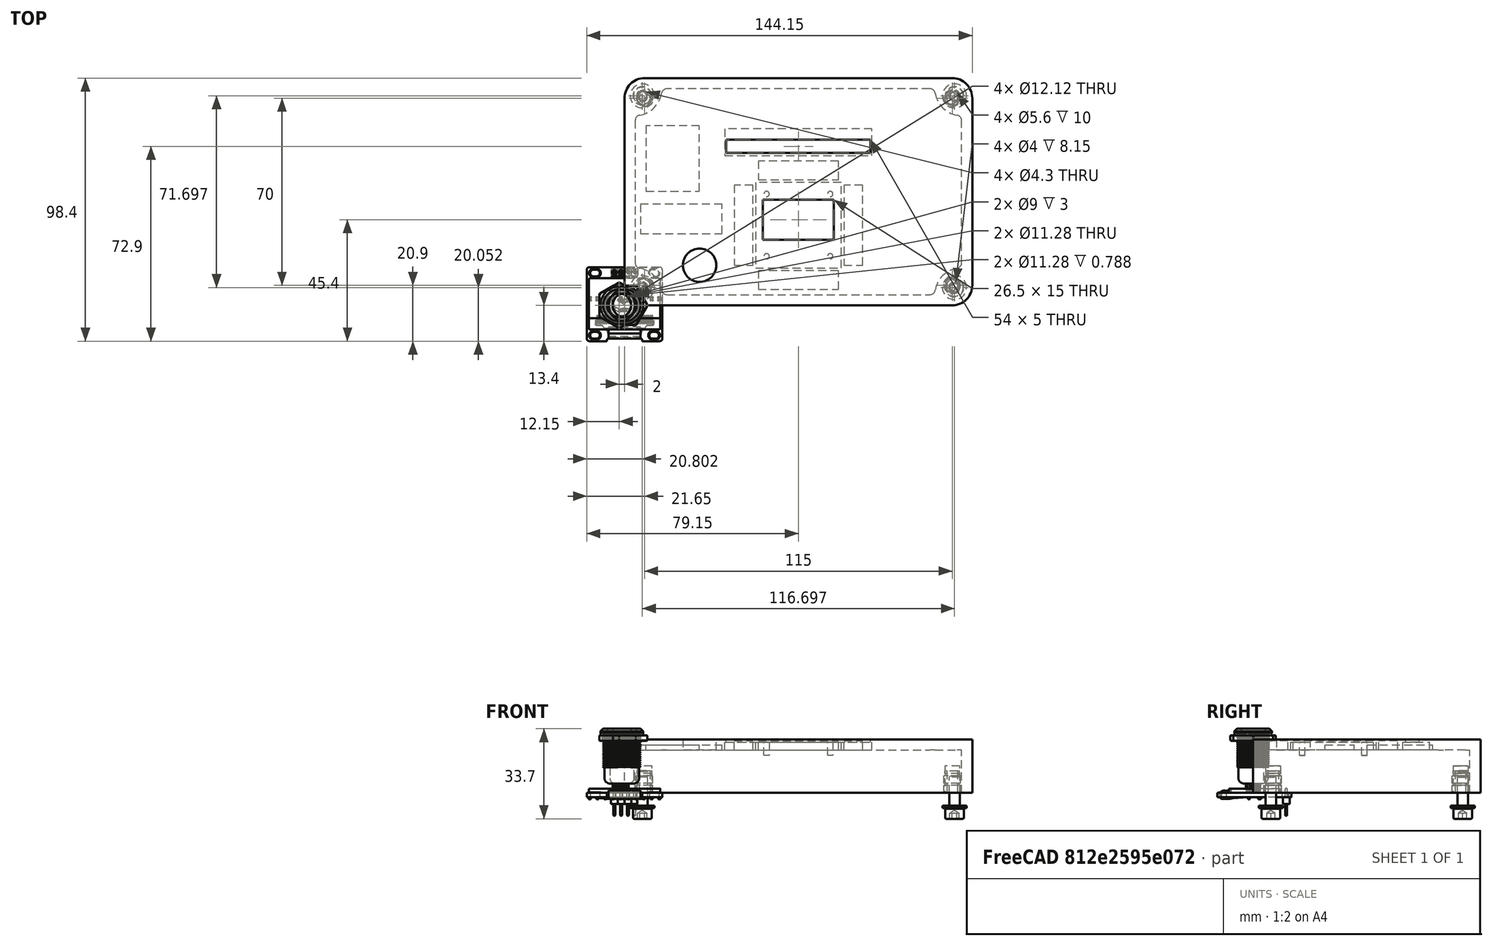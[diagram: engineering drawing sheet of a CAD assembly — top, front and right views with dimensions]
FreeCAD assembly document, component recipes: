
FREECAD ASSEMBLY — COMPONENT RECIPES ("FirstDraft")

This assembly document has 5 components, labeled P0..P4 below (a component is one placed body or linked part). 2 of them carry a construction recipe — the FreeCAD feature program that regenerates the part from scratch, quoted from this document or its linked companion documents; the rest are supplied as boundary geometry only. No exploded tour is included for this assembly.
COMPONENT P0 — geometry summary ("Assembly"; no construction recipe available for this part):
  bounding box: 130.0 x 85.0 x 30.0 mm
  tessellated surface: 3,268 triangles
  volume: 81614518091937392678094543782171779412625645482801444618089581424482953678321251914316762090945118208 mm^3 (24619764130297853257637544613362442512160034095616427615261483626677733875047030041199137435680768% of its bounding box)
  symmetry: mirror-symmetric across its x mid-plane
COMPONENT P1 — recipe-attached ("Base", modeled in this document).
Construction recipe (the document's own serialized feature program — sketch geometry with constraints, then the solid features built on it; lengths are millimeters unless a unit is written):

FEATURE [PartDesign::ShapeBinder] ShapeBinder
  Support = -> [Pocket]
  TraceSupport = true
FEATURE [Sketcher::SketchObject] Sketch010
  ExternalGeometry = -> [ShapeBinder]
  FullyConstrained = true
  MapMode = 5
  Placement = pos=(0,0,0) rot=(1,0,0;3.14159rad)
  Support = -> [ShapeBinder]
  sketch-geometry (23):
    g0: GeomPoint X=5 Y=-5 Z=0
    g1: GeomPoint X=125 Y=-80 Z=0
    g2: GeomPoint X=65 Y=-42.5 Z=0
    g3: ArcOfCircle CenterX=5 CenterY=-80 CenterZ=0 NormalX=0 NormalY=0 NormalZ=1 AngleXU=0 Radius=10 StartAngle=0.167448 EndAngle=1.40335
    g4: ArcOfCircle CenterX=7 CenterY=-68.1678 CenterZ=0 NormalX=0 NormalY=0 NormalZ=1 AngleXU=0 Radius=2 StartAngle=3.14159 EndAngle=4.54494
    g5: ArcOfCircle CenterX=5 CenterY=-5 CenterZ=0 NormalX=0 NormalY=0 NormalZ=1 AngleXU=0 Radius=10 StartAngle=1.40335 EndAngle=6.11574
    g6: ArcOfCircle CenterX=125 CenterY=-5 CenterZ=0 NormalX=0 NormalY=0 NormalZ=1 AngleXU=0 Radius=10 StartAngle=3.30904 EndAngle=4.54494
    g7: ArcOfCircle CenterX=125 CenterY=-80 CenterZ=0 NormalX=0 NormalY=0 NormalZ=1 AngleXU=0 Radius=10 StartAngle=1.73824 EndAngle=2.97414
    g8: LineSegment StartX=5 StartY=-80 StartZ=0 EndX=125 EndY=-80 EndZ=0
    g9: LineSegment StartX=125 StartY=-80 StartZ=0 EndX=125 EndY=-5 EndZ=0
    g10: LineSegment StartX=5 StartY=-5 StartZ=0 EndX=5 EndY=-80 EndZ=0
    g11: ArcOfCircle CenterX=7 CenterY=6.83216 CenterZ=0 NormalX=0 NormalY=0 NormalZ=1 AngleXU=0 Radius=2 StartAngle=4.54494 EndAngle=9.42478
    g12: ArcOfCircle CenterX=123 CenterY=-16.8322 CenterZ=0 NormalX=0 NormalY=0 NormalZ=1 AngleXU=0 Radius=2 StartAngle=4e-16 EndAngle=1.40335
    g13: ArcOfCircle CenterX=16.8322 CenterY=-7 CenterZ=0 NormalX=0 NormalY=0 NormalZ=1 AngleXU=0 Radius=2 StartAngle=1.5708 EndAngle=2.97414
    g14: ArcOfCircle CenterX=113.168 CenterY=-7 CenterZ=0 NormalX=0 NormalY=0 NormalZ=1 AngleXU=0 Radius=2 StartAngle=0.167448 EndAngle=1.5708
    g15: ArcOfCircle CenterX=123 CenterY=-68.1678 CenterZ=0 NormalX=0 NormalY=0 NormalZ=1 AngleXU=0 Radius=2 StartAngle=4.87984 EndAngle=6.28319
    g16: ArcOfCircle CenterX=113.168 CenterY=-78 CenterZ=0 NormalX=0 NormalY=0 NormalZ=1 AngleXU=0 Radius=2 StartAngle=4.71239 EndAngle=6.11574
    g17: ArcOfCircle CenterX=16.8322 CenterY=-78 CenterZ=0 NormalX=0 NormalY=0 NormalZ=1 AngleXU=0 Radius=2 StartAngle=3.30904 EndAngle=4.71239
    g18: LineSegment StartX=5 StartY=-5 StartZ=0 EndX=125 EndY=-5 EndZ=0
    g19: LineSegment StartX=5 StartY=6.83216 StartZ=0 EndX=5 EndY=-68.1678 EndZ=0
    g20: LineSegment StartX=125 StartY=-68.1678 StartZ=0 EndX=125 EndY=-16.8322 EndZ=0
    g21: LineSegment StartX=113.168 StartY=-5 StartZ=0 EndX=16.8322 EndY=-5 EndZ=0
    g22: LineSegment StartX=16.8322 StartY=-80 StartZ=0 EndX=113.168 EndY=-80 EndZ=0
  constraints (54):
    c: Tangent(g3,g4) = 1.5708
    c: Coincident(g7,g1)
    c: Coincident(g8,g9)
    c: Coincident(g10,g8)
    c: Horizontal(g8)
    c: Vertical(g9)
    c: Vertical(g10)
    c: Coincident(g8,g3)
    c: Coincident(g9,g6)
    c: Coincident(g0,g5)
    c: Symmetric(g3,g6,g2)
    c: Tangent(g5,g11) = 1.5708
    c: Tangent(g6,g12) = 1.5708
    c: Tangent(g5,g13) = 1.5708
    c: Tangent(g6,g14) = 1.5708
    c: Tangent(g7,g15) = 1.5708
    c: Tangent(g7,g16) = 1.5708
    c: Equal(g3,g5)
    c: Equal(g5,g6)
    c: Equal(g6,g7)
    c: Radius(g3) = 10
    c: Equal(g4,g13)
    c: Equal(g13,g11)
    c: Equal(g11,g14)
    c: Equal(g12,g15)
    c: Tangent(g16,g8) = -1.5708
    c: Tangent(g4,g10) = -1.5708
    c: Coincident(g8,g7)
    c: Tangent(g17,g8) = -1.5708
    c: Tangent(g17,g3) = 1.5708
    c: Radius(g17) = 2
    c: Tangent(g12,g9) = -1.5708
    c: Tangent(g15,g9) = -1.5708
    c: Tangent(g11,g10) = -1.5708
    c: Coincident(g18,g5)
    c: Horizontal(g18)
    c: Coincident(g18,g6)
    c: Coincident(g10,g5)
    c: Tangent(g13,g18) = 1.5708
    c: Tangent(g14,g18) = 1.5708
    c: Equal(g11,g12)
    c: Equal(g14,g17)
    c: Equal(g17,g16)
    c: Symmetric(g-3,g-5,g2)
    c: Coincident(g19,g11)
    c: Coincident(g19,g4)
    c: Coincident(g20,g15)
    c: Coincident(g20,g12)
    c: Coincident(g21,g14)
    c: Coincident(g21,g13)
    c: DistanceY(g5,g-4) = 1
    c: DistanceX(g-5,g11) = 1
    c: Coincident(g22,g17)
    c: Coincident(g22,g16)
FEATURE [Sketcher::SketchObject] Sketch011
  ExternalGeometry = -> [ShapeBinder]
  FullyConstrained = true
  MapMode = 5
  Placement = pos=(0,0,0) rot=(1,0,0;3.14159rad)
  Support = -> [ShapeBinder]
  sketch-geometry (12):
    g0: LineSegment StartX=7.5 StartY=0 StartZ=0 EndX=122.5 EndY=0 EndZ=0
    g1: LineSegment StartX=130 StartY=-7.5 StartZ=0 EndX=130 EndY=-77.5 EndZ=0
    g2: LineSegment StartX=122.5 StartY=-85 StartZ=0 EndX=7.5 EndY=-85 EndZ=0
    g3: LineSegment StartX=0 StartY=-77.5 StartZ=0 EndX=0 EndY=-7.5 EndZ=0
    g4: ArcOfCircle CenterX=7.5 CenterY=-7.5 CenterZ=0 NormalX=0 NormalY=0 NormalZ=1 AngleXU=0 Radius=7.5 StartAngle=1.5708 EndAngle=3.14159
    g5: GeomPoint X=0 Y=0 Z=0
    g6: ArcOfCircle CenterX=122.5 CenterY=-7.5 CenterZ=0 NormalX=0 NormalY=0 NormalZ=1 AngleXU=0 Radius=7.5 StartAngle=0 EndAngle=1.5708
    g7: GeomPoint X=130 Y=0 Z=0
    g8: ArcOfCircle CenterX=122.5 CenterY=-77.5 CenterZ=0 NormalX=0 NormalY=0 NormalZ=1 AngleXU=0 Radius=7.5 StartAngle=4.71239 EndAngle=6.28319
    g9: GeomPoint X=130 Y=-85 Z=0
    g10: ArcOfCircle CenterX=7.5 CenterY=-77.5 CenterZ=0 NormalX=0 NormalY=0 NormalZ=1 AngleXU=0 Radius=7.5 StartAngle=3.14159 EndAngle=4.71239
    g11: GeomPoint X=0 Y=-85 Z=0
  constraints (23):
    c: Horizontal(g0)
    c: Vertical(g1)
    c: Vertical(g3)
    c: Coincident(g5,g-1)
    c: PointOnObject(g5,g3)
    c: Tangent(g0,g4) = 1.5708
    c: Tangent(g3,g4) = 1.5708
    c: PointOnObject(g7,g1)
    c: PointOnObject(g7,g0)
    c: Tangent(g1,g6) = 1.5708
    c: Tangent(g0,g6) = 1.5708
    c: PointOnObject(g9,g1)
    c: PointOnObject(g9,g2)
    c: Tangent(g1,g8) = 1.5708
    c: Tangent(g2,g8) = 1.5708
    c: PointOnObject(g11,g2)
    c: PointOnObject(g11,g3)
    c: Tangent(g2,g10) = 1.5708
    c: Tangent(g3,g10) = 1.5708
    c: Coincident(g2,g-4)
    c: Coincident(g2,g-4)
    c: Coincident(g-3,g1)
    c: Coincident(g0,g-5)
FEATURE [PartDesign::Pad] Pad003
  Direction = (0,0,-1)
  Length = 10
  Length2 = 10
  Profile = -> Sketch011
  ReferenceAxis = -> Sketch011 [N_Axis]
  Type = 0
FEATURE [PartDesign::Pocket] Pocket005
  BaseFeature = -> Pad003
  Direction = (0,0,1)
  Length = 7
  Length2 = 5
  Profile = -> Sketch010
  ReferenceAxis = -> Sketch010 [N_Axis]
  Reversed = true
  Type = 0
FEATURE [Sketcher::SketchObject] Sketch012
  ExternalGeometry = -> [ShapeBinder]
  FullyConstrained = true
  MapMode = 5
  Placement = pos=(0,0,-10) rot=(1,0,0;3.14159rad)
  Support = -> [Pocket005]
  sketch-geometry (4):
    g0: Circle CenterX=6.65146 CenterY=-6.65148 CenterZ=0 NormalX=0 NormalY=0 NormalZ=1 AngleXU=0 Radius=2.8
    g1: Circle CenterX=123.349 CenterY=-6.65148 CenterZ=0 NormalX=0 NormalY=0 NormalZ=1 AngleXU=0 Radius=2.8
    g2: Circle CenterX=123.349 CenterY=-78.3485 CenterZ=0 NormalX=0 NormalY=0 NormalZ=1 AngleXU=0 Radius=2.8
    g3: Circle CenterX=6.65146 CenterY=-78.3485 CenterZ=0 NormalX=0 NormalY=0 NormalZ=1 AngleXU=0 Radius=2.8
  constraints (8):
    c: Coincident(g1,g-4)
    c: Coincident(g2,g-5)
    c: Coincident(g3,g-6)
    c: Coincident(g0,g-3)
    c: Equal(g0,g-3)
    c: Equal(g0,g1)
    c: Equal(g1,g2)
    c: Equal(g2,g3)
FEATURE [PartDesign::Hole] Hole
  BaseFeature = -> Pocket005
  CustomThreadClearance = 0
  Depth = 314.401
  DepthType = 1
  Diameter = 4.5
  DrillForDepth = false
  DrillPoint = 1
  DrillPointAngle = 118
  HoleCutCountersinkAngle = 90
  HoleCutCustomValues = false
  HoleCutDepth = 5.2
  HoleCutDiameter = 10
  HoleCutType = 12
  ModelThread = false
  Profile = -> Sketch012
  Tapered = false
  TaperedAngle = 90
  ThreadClass = 0
  ThreadDepth = 314.401
  ThreadDepthType = 0
  ThreadDirection = 0
  ThreadFit = 0
  ThreadSize = 11
  ThreadType = 1
  Threaded = false
  UseCustomThreadClearance = false
FEATURE [Sketcher::SketchObject] Sketch013
  ExternalGeometry = -> [ShapeBinder]
  FullyConstrained = true
  MapMode = 5
  Placement = pos=(0,0,0) rot=(1,0,0;3.14159rad)
  Support = -> [ShapeBinder]
  sketch-geometry (46):
    g0: GeomPoint X=5 Y=-28.6643 Z=0
    g1: GeomPoint X=125 Y=-80 Z=0
    g2: GeomPoint X=65 Y=-54.3322 Z=0
    g3: ArcOfCircle CenterX=5 CenterY=-80 CenterZ=0 NormalX=0 NormalY=0 NormalZ=1 AngleXU=0 Radius=10 StartAngle=0.167448 EndAngle=1.40335
    g4: ArcOfCircle CenterX=7 CenterY=-68.1678 CenterZ=0 NormalX=0 NormalY=0 NormalZ=1 AngleXU=0 Radius=2 StartAngle=3.14159 EndAngle=4.54494
    g5: ArcOfCircle CenterX=5 CenterY=-28.6643 CenterZ=0 NormalX=0 NormalY=0 NormalZ=1 AngleXU=0 Radius=10 StartAngle=4.87984 EndAngle=6.11574
    g6: ArcOfCircle CenterX=125 CenterY=-28.6643 CenterZ=0 NormalX=0 NormalY=0 NormalZ=1 AngleXU=0 Radius=10 StartAngle=3.30904 EndAngle=4.54494
    g7: ArcOfCircle CenterX=125 CenterY=-80 CenterZ=0 NormalX=0 NormalY=0 NormalZ=1 AngleXU=0 Radius=10 StartAngle=1.73824 EndAngle=2.97414
    g8: LineSegment StartX=5 StartY=-80 StartZ=0 EndX=125 EndY=-80 EndZ=0
    g9: LineSegment StartX=125 StartY=-80 StartZ=0 EndX=125 EndY=-28.6643 EndZ=0
    g10: LineSegment StartX=5 StartY=-28.6643 StartZ=0 EndX=5 EndY=-80 EndZ=0
    g11: ArcOfCircle CenterX=7 CenterY=-40.4965 CenterZ=0 NormalX=0 NormalY=0 NormalZ=1 AngleXU=0 Radius=2 StartAngle=1.73824 EndAngle=3.14159
    g12: ArcOfCircle CenterX=123 CenterY=-40.4965 CenterZ=0 NormalX=0 NormalY=0 NormalZ=1 AngleXU=0 Radius=2 StartAngle=-9e-16 EndAngle=1.40335
    g13: ArcOfCircle CenterX=16.8322 CenterY=-30.6643 CenterZ=0 NormalX=0 NormalY=0 NormalZ=1 AngleXU=0 Radius=2 StartAngle=1.5708 EndAngle=2.97414
    g14: ArcOfCircle CenterX=113.168 CenterY=-30.6643 CenterZ=0 NormalX=0 NormalY=0 NormalZ=1 AngleXU=0 Radius=2 StartAngle=0.167448 EndAngle=1.5708
    g15: ArcOfCircle CenterX=123 CenterY=-68.1678 CenterZ=0 NormalX=0 NormalY=0 NormalZ=1 AngleXU=0 Radius=2 StartAngle=4.87984 EndAngle=6.28319
    g16: ArcOfCircle CenterX=113.168 CenterY=-78 CenterZ=0 NormalX=0 NormalY=0 NormalZ=1 AngleXU=0 Radius=2 StartAngle=4.71239 EndAngle=6.11574
    g17: ArcOfCircle CenterX=16.8322 CenterY=-78 CenterZ=0 NormalX=0 NormalY=0 NormalZ=1 AngleXU=0 Radius=2 StartAngle=3.30904 EndAngle=4.71239
    g18: LineSegment StartX=5 StartY=-28.6643 StartZ=0 EndX=125 EndY=-28.6643 EndZ=0
    g19: LineSegment StartX=5 StartY=-40.4965 StartZ=0 EndX=5 EndY=-68.1678 EndZ=0
    g20: LineSegment StartX=125 StartY=-68.1678 StartZ=0 EndX=125 EndY=-40.4965 EndZ=0
    g21: LineSegment StartX=113.168 StartY=-28.6643 StartZ=0 EndX=16.8322 EndY=-28.6643 EndZ=0
    g22: LineSegment StartX=16.8322 StartY=-80 StartZ=0 EndX=113.168 EndY=-80 EndZ=0
    g23: GeomPoint X=4 Y=-27.6643 Z=0
    g24: GeomPoint X=126 Y=-81 Z=0
    g25: GeomPoint X=65 Y=-54.3322 Z=0
    g26: ArcOfCircle CenterX=4 CenterY=-81 CenterZ=0 NormalX=0 NormalY=0 NormalZ=1 AngleXU=0 Radius=10 StartAngle=0.167448 EndAngle=1.40335
    g27: ArcOfCircle CenterX=6 CenterY=-69.1678 CenterZ=0 NormalX=0 NormalY=0 NormalZ=1 AngleXU=0 Radius=2 StartAngle=3.14159 EndAngle=4.54494
    g28: ArcOfCircle CenterX=4 CenterY=-27.6643 CenterZ=0 NormalX=0 NormalY=0 NormalZ=1 AngleXU=0 Radius=10 StartAngle=1.40335 EndAngle=6.11574
    g29: ArcOfCircle CenterX=126 CenterY=-27.6643 CenterZ=0 NormalX=0 NormalY=0 NormalZ=1 AngleXU=0 Radius=10 StartAngle=3.30904 EndAngle=4.54494
    g30: ArcOfCircle CenterX=126 CenterY=-81 CenterZ=0 NormalX=0 NormalY=0 NormalZ=1 AngleXU=0 Radius=10 StartAngle=1.73824 EndAngle=2.97414
    g31: LineSegment StartX=4 StartY=-81 StartZ=0 EndX=126 EndY=-81 EndZ=0
    g32: LineSegment StartX=126 StartY=-81 StartZ=0 EndX=126 EndY=-27.6643 EndZ=0
    g33: LineSegment StartX=4 StartY=-27.6643 StartZ=0 EndX=4 EndY=-81 EndZ=0
    g34: ArcOfCircle CenterX=6 CenterY=-15.8322 CenterZ=0 NormalX=0 NormalY=0 NormalZ=1 AngleXU=0 Radius=2 StartAngle=4.54494 EndAngle=9.42478
    g35: ArcOfCircle CenterX=124 CenterY=-39.4965 CenterZ=0 NormalX=0 NormalY=0 NormalZ=1 AngleXU=0 Radius=2 StartAngle=-9e-16 EndAngle=1.40335
    g36: ArcOfCircle CenterX=15.8322 CenterY=-29.6643 CenterZ=0 NormalX=0 NormalY=0 NormalZ=1 AngleXU=0 Radius=2 StartAngle=1.5708 EndAngle=2.97414
    g37: ArcOfCircle CenterX=114.168 CenterY=-29.6643 CenterZ=0 NormalX=0 NormalY=0 NormalZ=1 AngleXU=0 Radius=2 StartAngle=0.167448 EndAngle=1.5708
    g38: ArcOfCircle CenterX=124 CenterY=-69.1678 CenterZ=0 NormalX=0 NormalY=0 NormalZ=1 AngleXU=0 Radius=2 StartAngle=4.87984 EndAngle=6.28319
    g39: ArcOfCircle CenterX=114.168 CenterY=-79 CenterZ=0 NormalX=0 NormalY=0 NormalZ=1 AngleXU=0 Radius=2 StartAngle=4.71239 EndAngle=6.11574
    g40: ArcOfCircle CenterX=15.8322 CenterY=-79 CenterZ=0 NormalX=0 NormalY=0 NormalZ=1 AngleXU=0 Radius=2 StartAngle=3.30904 EndAngle=4.71239
    g41: LineSegment StartX=4 StartY=-27.6643 StartZ=0 EndX=126 EndY=-27.6643 EndZ=0
    g42: LineSegment StartX=4 StartY=-15.8322 StartZ=0 EndX=4 EndY=-69.1678 EndZ=0
    g43: LineSegment StartX=126 StartY=-69.1678 StartZ=0 EndX=126 EndY=-39.4965 EndZ=0
    g44: LineSegment StartX=114.168 StartY=-27.6643 StartZ=0 EndX=15.8322 EndY=-27.6643 EndZ=0
    g45: LineSegment StartX=15.8322 StartY=-81 StartZ=0 EndX=114.168 EndY=-81 EndZ=0
  constraints (107):
    c: Tangent(g3,g4) = 1.5708
    c: Coincident(g7,g1)
    c: Coincident(g8,g9)
    c: Coincident(g10,g8)
    c: Horizontal(g8)
    c: Vertical(g9)
    c: Vertical(g10)
    c: Coincident(g8,g3)
    c: Coincident(g9,g6)
    c: Coincident(g0,g5)
    c: Symmetric(g3,g6,g2)
    c: Tangent(g5,g11) = 1.5708
    c: Tangent(g6,g12) = 1.5708
    c: Tangent(g5,g13) = 1.5708
    c: Tangent(g6,g14) = 1.5708
    c: Tangent(g7,g15) = 1.5708
    c: Tangent(g7,g16) = 1.5708
    c: Equal(g3,g5)
    c: Equal(g5,g6)
    c: Equal(g6,g7)
    c: Radius(g3) = 10
    c: Equal(g4,g13)
    c: Equal(g13,g11)
    c: Equal(g11,g14)
    c: Equal(g12,g15)
    c: Tangent(g16,g8) = -1.5708
    c: Tangent(g4,g10) = -1.5708
    c: Coincident(g8,g7)
    c: Tangent(g17,g8) = -1.5708
    c: Tangent(g17,g3) = 1.5708
    c: Radius(g17) = 2
    c: Tangent(g12,g9) = -1.5708
    c: Tangent(g15,g9) = -1.5708
    c: Tangent(g11,g10) = -1.5708
    c: Coincident(g18,g5)
    c: Horizontal(g18)
    c: Coincident(g18,g6)
    c: Coincident(g10,g5)
    c: Tangent(g13,g18) = 1.5708
    c: Tangent(g14,g18) = 1.5708
    c: Equal(g11,g12)
    c: Equal(g14,g17)
    c: Equal(g17,g16)
    c: Coincident(g19,g11)
    c: Coincident(g19,g4)
    c: Coincident(g20,g15)
    c: Coincident(g20,g12)
    c: Coincident(g21,g14)
    c: Coincident(g21,g13)
    c: Coincident(g22,g17)
    c: Coincident(g22,g16)
    c: Tangent(g26,g27) = 1.5708
    c: Coincident(g30,g24)
    c: Coincident(g31,g32)
    c: Coincident(g33,g31)
    c: Horizontal(g31)
    c: Vertical(g32)
    c: Vertical(g33)
    c: Coincident(g31,g26)
    c: Coincident(g32,g29)
    c: Coincident(g23,g28)
    c: Symmetric(g26,g29,g25)
    c: Tangent(g28,g34) = 1.5708
    c: Tangent(g29,g35) = 1.5708
    c: Tangent(g28,g36) = 1.5708
    c: Tangent(g29,g37) = 1.5708
    c: Tangent(g30,g38) = 1.5708
    c: Tangent(g30,g39) = 1.5708
    c: Equal(g26,g28)
    c: Equal(g28,g29)
    c: Equal(g29,g30)
    c: Radius(g26) = 10
    c: Equal(g27,g36)
    c: Equal(g36,g34)
    c: Equal(g34,g37)
    c: Equal(g35,g38)
    c: Tangent(g39,g31) = -1.5708
    c: Tangent(g27,g33) = -1.5708
    c: Coincident(g31,g30)
    c: Tangent(g40,g31) = -1.5708
    c: Tangent(g40,g26) = 1.5708
    c: Radius(g40) = 2
    c: Tangent(g35,g32) = -1.5708
    c: Tangent(g38,g32) = -1.5708
    c: Tangent(g34,g33) = -1.5708
    c: Coincident(g41,g28)
    c: Horizontal(g41)
    c: Coincident(g41,g29)
    c: Coincident(g33,g28)
    c: Tangent(g36,g41) = 1.5708
    c: Tangent(g37,g41) = 1.5708
    c: Equal(g34,g35)
    c: Equal(g37,g40)
    c: Equal(g40,g39)
    c: Coincident(g42,g34)
    c: Coincident(g42,g27)
    c: Coincident(g43,g38)
    c: Coincident(g43,g35)
    c: Coincident(g44,g37)
    c: Coincident(g44,g36)
    c: Coincident(g45,g40)
    c: Coincident(g45,g39)
    c: Symmetric(g28,g30,g2)
    c: Coincident(g34,g-3)
    c: Coincident(g38,g-4)
    c: DistanceX(g27,g4) = 1
    c: DistanceY(g40,g17) = 1
FEATURE [PartDesign::Pad] Pad004
  BaseFeature = -> Hole
  Direction = (0,0,-1)
  Length = 10
  Length2 = 10
  Profile = -> Sketch013
  ReferenceAxis = -> Sketch013 [N_Axis]
  Reversed = true
  Type = 0
FEATURE [PartDesign::CoordinateSystem] LCS_1
  AttacherType = Attacher::AttachEngine3D
  MapMode = 5
  Support = -> [Pad004]
FEATURE [PartDesign::Line] HoleAxis_1
  AttacherType = Attacher::AttachEngineLine
  Length = 4.79083
  MapMode = 19
  Placement = pos=(123.349,6.65148,-4.8) rot=(0,1,0;3.14159rad)
  ResizeMode = 1
  Support = -> [Pad004]
FEATURE [PartDesign::Line] HoleAxis_2
  AttacherType = Attacher::AttachEngineLine
  Length = 4.79083
  MapMode = 19
  Placement = pos=(123.349,78.3485,-4.8) rot=(0,1,0;3.14159rad)
  ResizeMode = 1
  Support = -> [Pad004]
FEATURE [PartDesign::Line] HoleAxis_3
  AttacherType = Attacher::AttachEngineLine
  Length = 4.79083
  MapMode = 19
  Placement = pos=(6.65146,78.3485,-4.8) rot=(0,1,0;3.14159rad)
  ResizeMode = 1
  Support = -> [Pad004]
FEATURE [PartDesign::Line] HoleAxis_4
  AttacherType = Attacher::AttachEngineLine
  Length = 4.79083
  MapMode = 19
  Placement = pos=(6.65146,6.65148,-4.8) rot=(0,1,0;3.14159rad)
  ResizeMode = 1
  Support = -> [Pad004]
FEATURE [PartDesign::Body] Body  label="Base"
  Group = -> [ShapeBinder,Sketch010,Sketch011,Pad003,Pocket005,Sketch012,Hole,Sketch013,Pad004,LCS_1,HoleAxis_1,HoleAxis_2,HoleAxis_3,HoleAxis_4]
  Origin = -> Origin
  Tip = -> Pad004
COMPONENT P2 — geometry summary ("Double-Switch"; no construction recipe available for this part):
  bounding box: 32.9 x 23.8 x 17.0 mm
  tessellated surface: 5,444 triangles
  volume: 4589 mm^3 (34% of its bounding box)
COMPONENT P3 — recipe-attached ("Front inkl. Fasteners", modeled in this document).
Construction recipe (the document's own serialized feature program — sketch geometry with constraints, then the solid features built on it; lengths are millimeters unless a unit is written):

FEATURE [PartDesign::AdditiveBox] Box002
  AttacherType = Attacher::AttachEngine3D
  Height = 20
  Length = 130
  Width = 85
FEATURE [Sketcher::SketchObject] Sketch001
  ExternalGeometry = -> [Box002]
  FullyConstrained = true
  MapMode = 5
  Placement = pos=(0,0,0) rot=(1,0,0;3.14159rad)
  Support = -> [Box002]
  sketch-geometry (23):
    g0: LineSegment StartX=15.8322 StartY=-4 StartZ=0 EndX=114.168 EndY=-4 EndZ=0
    g1: LineSegment StartX=126 StartY=-15.8322 StartZ=0 EndX=126 EndY=-69.1678 EndZ=0
    g2: LineSegment StartX=114.168 StartY=-81 StartZ=0 EndX=15.8322 EndY=-81 EndZ=0
    g3: LineSegment StartX=4 StartY=-69.1678 StartZ=0 EndX=4 EndY=-15.8322 EndZ=0
    g4: GeomPoint X=4 Y=-4 Z=0
    g5: GeomPoint X=126 Y=-81 Z=0
    g6: GeomPoint X=65 Y=-42.5 Z=0
    g7: ArcOfCircle CenterX=4 CenterY=-81 CenterZ=0 NormalX=0 NormalY=0 NormalZ=1 AngleXU=0 Radius=10 StartAngle=0.167448 EndAngle=1.40335
    g8: ArcOfCircle CenterX=6 CenterY=-69.1678 CenterZ=0 NormalX=0 NormalY=0 NormalZ=1 AngleXU=0 Radius=2 StartAngle=3.14159 EndAngle=4.54494
    g9: ArcOfCircle CenterX=15.8322 CenterY=-79 CenterZ=0 NormalX=0 NormalY=0 NormalZ=1 AngleXU=0 Radius=2 StartAngle=3.30904 EndAngle=4.71239
    g10: ArcOfCircle CenterX=4 CenterY=-4 CenterZ=0 NormalX=0 NormalY=0 NormalZ=1 AngleXU=0 Radius=10 StartAngle=4.87984 EndAngle=6.11574
    g11: ArcOfCircle CenterX=126 CenterY=-4 CenterZ=0 NormalX=0 NormalY=0 NormalZ=1 AngleXU=0 Radius=10 StartAngle=3.30904 EndAngle=4.54494
    g12: ArcOfCircle CenterX=126 CenterY=-81 CenterZ=0 NormalX=0 NormalY=0 NormalZ=1 AngleXU=0 Radius=10 StartAngle=1.73824 EndAngle=2.97414
    g13: LineSegment StartX=4 StartY=-81 StartZ=0 EndX=126 EndY=-81 EndZ=0
    g14: LineSegment StartX=126 StartY=-81 StartZ=0 EndX=126 EndY=-4 EndZ=0
    g15: LineSegment StartX=126 StartY=-4 StartZ=0 EndX=4 EndY=-4 EndZ=0
    g16: LineSegment StartX=4 StartY=-4 StartZ=0 EndX=4 EndY=-81 EndZ=0
    g17: ArcOfCircle CenterX=6 CenterY=-15.8322 CenterZ=0 NormalX=0 NormalY=0 NormalZ=1 AngleXU=0 Radius=2 StartAngle=1.73824 EndAngle=3.14159
    g18: ArcOfCircle CenterX=124 CenterY=-15.8322 CenterZ=0 NormalX=0 NormalY=0 NormalZ=1 AngleXU=0 Radius=2 StartAngle=0 EndAngle=1.40335
    g19: ArcOfCircle CenterX=15.8322 CenterY=-6 CenterZ=0 NormalX=0 NormalY=0 NormalZ=1 AngleXU=0 Radius=2 StartAngle=1.5708 EndAngle=2.97414
    g20: ArcOfCircle CenterX=114.168 CenterY=-6 CenterZ=0 NormalX=0 NormalY=0 NormalZ=1 AngleXU=0 Radius=2 StartAngle=0.167448 EndAngle=1.5708
    g21: ArcOfCircle CenterX=124 CenterY=-69.1678 CenterZ=0 NormalX=0 NormalY=0 NormalZ=1 AngleXU=0 Radius=2 StartAngle=4.87984 EndAngle=6.28319
    g22: ArcOfCircle CenterX=114.168 CenterY=-79 CenterZ=0 NormalX=0 NormalY=0 NormalZ=1 AngleXU=0 Radius=2 StartAngle=4.71239 EndAngle=6.11574
  constraints (56):
    c: Horizontal(g0)
    c: Horizontal(g2)
    c: Vertical(g1)
    c: Vertical(g3)
    c: PointOnObject(g4,g0)
    c: PointOnObject(g4,g3)
    c: PointOnObject(g5,g1)
    c: PointOnObject(g5,g2)
    c: Symmetric(g-6,g-4,g6)
    c: Tangent(g7,g8) = 1.5708
    c: Tangent(g3,g8) = 1.5708
    c: Tangent(g2,g9) = 1.5708
    c: Tangent(g7,g9) = 1.5708
    c: Coincident(g12,g5)
    c: Coincident(g13,g14)
    c: Coincident(g14,g15)
    c: Coincident(g15,g16)
    c: Coincident(g16,g13)
    c: Horizontal(g13)
    c: Horizontal(g15)
    c: Vertical(g14)
    c: Vertical(g16)
    c: Coincident(g13,g7)
    c: Coincident(g14,g11)
    c: Coincident(g4,g10)
    c: Symmetric(g7,g11,g6)
    c: Tangent(g3,g17) = 1.5708
    c: Tangent(g10,g17) = 1.5708
    c: Tangent(g1,g18) = 1.5708
    c: Tangent(g11,g18) = 1.5708
    c: Tangent(g10,g19) = 1.5708
    c: Tangent(g0,g19) = 1.5708
    c: Tangent(g11,g20) = 1.5708
    c: Tangent(g0,g20) = 1.5708
    c: Tangent(g1,g21) = 1.5708
    c: Tangent(g12,g21) = 1.5708
    c: Tangent(g2,g22) = 1.5708
    c: Tangent(g12,g22) = 1.5708
    c: PointOnObject(g0,g15)
    c: PointOnObject(g3,g16)
    c: PointOnObject(g1,g14)
    c: DistanceX(g-6,g7) = 4
    c: DistanceY(g-6,g7) = 4
    c: PointOnObject(g2,g13)
    c: Equal(g7,g10)
    c: Equal(g10,g11)
    c: Equal(g11,g12)
    c: Radius(g7) = 10
    c: Equal(g9,g8)
    c: Equal(g8,g19)
    c: Equal(g19,g17)
    c: Equal(g17,g20)
    c: Equal(g20,g18)
    c: Equal(g18,g21)
    c: Equal(g21,g22)
    c: Radius(g9) = 2
FEATURE [PartDesign::Pocket] Pocket001
  BaseFeature = -> Box002
  Direction = (0,0,1)
  Length = 16
  Length2 = 100
  Profile = -> Sketch001
  ReferenceAxis = -> Sketch001 [N_Axis]
  Type = 0
  expr: Length = <<Box002>>.Height - 4mm
FEATURE [Sketcher::SketchObject] Sketch002
  ExternalGeometry = -> [Pocket001]
  FullyConstrained = true
  MapMode = 5
  Placement = pos=(0,0,16) rot=(1,0,0;3.14159rad)
  Support = -> [Pocket001]
  sketch-geometry (11):
    g0: LineSegment StartX=49 StartY=-14 StartZ=0 EndX=81 EndY=-14 EndZ=0
    g1: LineSegment StartX=81 StartY=-14 StartZ=0 EndX=81 EndY=-46 EndZ=0
    g2: LineSegment StartX=81 StartY=-46 StartZ=0 EndX=49 EndY=-46 EndZ=0
    g3: LineSegment StartX=49 StartY=-46 StartZ=0 EndX=49 EndY=-14 EndZ=0
    g4: GeomPoint X=65 Y=-4 Z=0
    g5: LineSegment StartX=65 StartY=-4 StartZ=0 EndX=65 EndY=-14 EndZ=0
    g6: LineSegment StartX=37.5 StartY=-56 StartZ=0 EndX=92.5 EndY=-56 EndZ=0
    g7: LineSegment StartX=92.5 StartY=-56 StartZ=0 EndX=92.5 EndY=-66 EndZ=0
    g8: LineSegment StartX=92.5 StartY=-66 StartZ=0 EndX=37.5 EndY=-66 EndZ=0
    g9: LineSegment StartX=37.5 StartY=-66 StartZ=0 EndX=37.5 EndY=-56 EndZ=0
    g10: LineSegment StartX=65 StartY=-14 StartZ=0 EndX=65 EndY=-56 EndZ=0
  constraints (29):
    c: Coincident(g0,g1)
    c: Coincident(g1,g2)
    c: Coincident(g2,g3)
    c: Coincident(g3,g0)
    c: Horizontal(g0)
    c: Horizontal(g2)
    c: Vertical(g1)
    c: Vertical(g3)
    c: Coincident(g5,g4)
    c: Vertical(g5)
    c: Symmetric(g0,g0,g5)
    c: DistanceY(g5,g5) = 10
    c: DistanceY(g1,g1) = 32
    c: Equal(g1,g0)
    c: Coincident(g6,g7)
    c: Coincident(g7,g8)
    c: Coincident(g8,g9)
    c: Coincident(g9,g6)
    c: Horizontal(g6)
    c: Horizontal(g8)
    c: Vertical(g7)
    c: Vertical(g9)
    c: DistanceX(g6,g6) = 55
    c: DistanceY(g7,g7) = 10
    c: Coincident(g10,g5)
    c: Vertical(g10)
    c: Symmetric(g6,g6,g10)
    c: DistanceY(g6,g1) = 10
    c: Symmetric(g-3,g-3,g4)
FEATURE [PartDesign::Pocket] Pocket002  label="Platz OLED und LED-Strip"
  BaseFeature = -> Pocket001
  Direction = (0,0,1)
  Length = 3
  Length2 = 100
  Profile = -> Sketch002
  Type = 0
FEATURE [Sketcher::SketchObject] Sketch003
  ExternalGeometry = -> [Sketch002,Pocket002]
  FullyConstrained = true
  MapMode = 5
  Placement = pos=(0,0,16) rot=(1,0,0;3.14159rad)
  Support = -> [Pocket002]
  sketch-geometry (10):
    g0: LineSegment StartX=51.75 StartY=-24.5 StartZ=0 EndX=78.25 EndY=-24.5 EndZ=0
    g1: LineSegment StartX=78.25 StartY=-24.5 StartZ=0 EndX=78.25 EndY=-39.5 EndZ=0
    g2: LineSegment StartX=78.25 StartY=-39.5 StartZ=0 EndX=51.75 EndY=-39.5 EndZ=0
    g3: LineSegment StartX=51.75 StartY=-39.5 StartZ=0 EndX=51.75 EndY=-24.5 EndZ=0
    g4: LineSegment StartX=38 StartY=-57 StartZ=0 EndX=92 EndY=-57 EndZ=0
    g5: LineSegment StartX=92 StartY=-57 StartZ=0 EndX=92 EndY=-62 EndZ=0
    g6: LineSegment StartX=92 StartY=-62 StartZ=0 EndX=38 EndY=-62 EndZ=0
    g7: LineSegment StartX=38 StartY=-62 StartZ=0 EndX=38 EndY=-57 EndZ=0
    g8: LineSegment StartX=65 StartY=-57 StartZ=0 EndX=65 EndY=-56 EndZ=0
    g9: LineSegment StartX=65 StartY=-24.5 StartZ=0 EndX=65 EndY=-14 EndZ=0
  constraints (28):
    c: Coincident(g0,g1)
    c: Coincident(g1,g2)
    c: Coincident(g2,g3)
    c: Coincident(g3,g0)
    c: Horizontal(g0)
    c: Horizontal(g2)
    c: Vertical(g1)
    c: Vertical(g3)
    c: DistanceX(g0,g0) = 26.5
    c: DistanceY(g1,g1) = 15
    c: Coincident(g4,g5)
    c: Coincident(g5,g6)
    c: Coincident(g6,g7)
    c: Coincident(g7,g4)
    c: Horizontal(g4)
    c: Horizontal(g6)
    c: Vertical(g5)
    c: Vertical(g7)
    c: DistanceX(g4,g-3) = 0.5
    c: Vertical(g8)
    c: Symmetric(g4,g4,g8)
    c: Symmetric(g-3,g-4,g8)
    c: DistanceY(g5,g5) = 5
    c: DistanceY(g4,g-3) = 1
    c: Vertical(g9)
    c: Symmetric(g0,g0,g9)
    c: DistanceY(g9,g9) = 10.5
    c: Symmetric(g-5,g-5,g9)
FEATURE [PartDesign::Pocket] Pocket003  label="Sichtausschnitt"
  BaseFeature = -> Pocket002
  Direction = (0,0,1)
  Length = 1.01
  Length2 = 100
  Profile = -> Sketch003
  ReferenceAxis = -> Sketch003 [N_Axis]
  Type = 1
FEATURE [Sketcher::SketchObject] Sketch004  label="Sketch Halter OLED"
  ExternalGeometry = -> [Sketch002]
  FullyConstrained = true
  MapMode = 5
  Placement = pos=(0,0,19) rot=(1,0,0;3.14159rad)
  Support = -> [Pocket003]
  sketch-geometry (9):
    g0: Circle CenterX=53.1 CenterY=-18.35 CenterZ=0 NormalX=0 NormalY=0 NormalZ=1 AngleXU=0 Radius=1
    g1: Circle CenterX=76.9 CenterY=-18.35 CenterZ=0 NormalX=0 NormalY=0 NormalZ=1 AngleXU=0 Radius=1
    g2: Circle CenterX=76.9 CenterY=-41.65 CenterZ=0 NormalX=0 NormalY=0 NormalZ=1 AngleXU=0 Radius=1
    g3: Circle CenterX=53.1 CenterY=-41.65 CenterZ=0 NormalX=0 NormalY=0 NormalZ=1 AngleXU=0 Radius=1
    g4: LineSegment StartX=53.1 StartY=-18.35 StartZ=0 EndX=76.9 EndY=-18.35 EndZ=0
    g5: LineSegment StartX=76.9 StartY=-18.35 StartZ=0 EndX=76.9 EndY=-41.65 EndZ=0
    g6: LineSegment StartX=76.9 StartY=-41.65 StartZ=0 EndX=53.1 EndY=-41.65 EndZ=0
    g7: LineSegment StartX=53.1 StartY=-41.65 StartZ=0 EndX=53.1 EndY=-18.35 EndZ=0
    g8: GeomPoint X=65 Y=-30 Z=0
  constraints (20):
    c: Coincident(g4,g5)
    c: Coincident(g5,g6)
    c: Coincident(g6,g7)
    c: Coincident(g7,g4)
    c: Horizontal(g4)
    c: Horizontal(g6)
    c: Vertical(g5)
    c: Vertical(g7)
    c: Coincident(g4,g0)
    c: Coincident(g5,g2)
    c: Coincident(g1,g4)
    c: Coincident(g3,g6)
    c: Equal(g0,g1)
    c: Equal(g1,g2)
    c: Equal(g2,g3)
    c: Diameter(g1) = 2
    c: DistanceX(g4,g4) = 23.8
    c: DistanceY(g5,g5) = 23.3
    c: Symmetric(g-4,g-6,g8)
    c: Symmetric(g3,g1,g8)
FEATURE [PartDesign::Pad] Pad  label="Halter OLED"
  BaseFeature = -> Pocket003
  Direction = (0,0,-1)
  Length = 5
  Length2 = 100
  Profile = -> Sketch004
  ReferenceAxis = -> Sketch004 [N_Axis]
  Type = 0
FEATURE [Sketcher::SketchObject] Sketch005
  ExternalGeometry = -> [Sketch002]
  FullyConstrained = true
  MapMode = 5
  Placement = pos=(0,0,16) rot=(1,0,0;3.14159rad)
  Support = -> [Pad]
  sketch-geometry (26):
    g0: LineSegment StartX=50 StartY=-6 StartZ=0 EndX=80 EndY=-6 EndZ=0
    g1: LineSegment StartX=80 StartY=-6 StartZ=0 EndX=80 EndY=-13 EndZ=0
    g2: LineSegment StartX=80 StartY=-13 StartZ=0 EndX=50 EndY=-13 EndZ=0
    g3: LineSegment StartX=50 StartY=-13 StartZ=0 EndX=50 EndY=-6 EndZ=0
    g4: LineSegment StartX=82 StartY=-15 StartZ=0 EndX=89 EndY=-15 EndZ=0
    g5: LineSegment StartX=89 StartY=-15 StartZ=0 EndX=89 EndY=-45 EndZ=0
    g6: LineSegment StartX=89 StartY=-45 StartZ=0 EndX=82 EndY=-45 EndZ=0
    g7: LineSegment StartX=82 StartY=-45 StartZ=0 EndX=82 EndY=-15 EndZ=0
    g8: LineSegment StartX=41 StartY=-15 StartZ=0 EndX=48 EndY=-15 EndZ=0
    g9: LineSegment StartX=48 StartY=-15 StartZ=0 EndX=48 EndY=-45 EndZ=0
    g10: LineSegment StartX=48 StartY=-45 StartZ=0 EndX=41 EndY=-45 EndZ=0
    g11: LineSegment StartX=41 StartY=-45 StartZ=0 EndX=41 EndY=-15 EndZ=0
    g12: LineSegment StartX=50 StartY=-47 StartZ=0 EndX=80 EndY=-47 EndZ=0
    g13: LineSegment StartX=80 StartY=-47 StartZ=0 EndX=80 EndY=-54 EndZ=0
    g14: LineSegment StartX=80 StartY=-54 StartZ=0 EndX=50 EndY=-54 EndZ=0
    g15: LineSegment StartX=50 StartY=-54 StartZ=0 EndX=50 EndY=-47 EndZ=0
    g16: LineSegment StartX=48 StartY=-13 StartZ=0 EndX=82 EndY=-13 EndZ=0
    g17: LineSegment StartX=82 StartY=-13 StartZ=0 EndX=82 EndY=-47 EndZ=0
    g18: LineSegment StartX=82 StartY=-47 StartZ=0 EndX=48 EndY=-47 EndZ=0
    g19: LineSegment StartX=48 StartY=-47 StartZ=0 EndX=48 EndY=-13 EndZ=0
    g20: GeomPoint X=65 Y=-30 Z=0
    g21: GeomPoint X=48 Y=-30 Z=0
    g22: GeomPoint X=116 Y=-13 Z=0
    g23: GeomPoint X=82 Y=-30 Z=0
    g24: GeomPoint X=65 Y=-47 Z=0
    g25: GeomPoint X=65 Y=-13 Z=0
  constraints (61):
    c: Coincident(g0,g1)
    c: Coincident(g1,g2)
    c: Coincident(g2,g3)
    c: Coincident(g3,g0)
    c: Horizontal(g0)
    c: Horizontal(g2)
    c: Vertical(g1)
    c: Vertical(g3)
    c: Coincident(g4,g5)
    c: Coincident(g5,g6)
    c: Coincident(g6,g7)
    c: Coincident(g7,g4)
    c: Horizontal(g4)
    c: Horizontal(g6)
    c: Vertical(g5)
    c: Vertical(g7)
    c: Coincident(g8,g9)
    c: Coincident(g9,g10)
    c: Coincident(g10,g11)
    c: Coincident(g11,g8)
    c: Horizontal(g8)
    c: Horizontal(g10)
    c: Vertical(g9)
    c: Vertical(g11)
    c: Coincident(g12,g13)
    c: Coincident(g13,g14)
    c: Coincident(g14,g15)
    c: Coincident(g15,g12)
    c: Horizontal(g12)
    c: Horizontal(g14)
    c: Vertical(g13)
    c: Vertical(g15)
    c: Equal(g4,g1)
    c: Equal(g1,g8)
    c: Equal(g8,g13)
    c: Coincident(g16,g17)
    c: Coincident(g17,g18)
    c: Coincident(g18,g19)
    c: Coincident(g19,g16)
    c: DistanceX(g-4,g16) = 1
    c: DistanceY(g-4,g16) = 1
    c: Symmetric(g16,g18,g20)
    c: Symmetric(g-6,g-4,g20)
    c: DistanceY(g15,g15) = 7
    c: Vertical(g19)
    c: Horizontal(g16)
    c: PointOnObject(g12,g18)
    c: Vertical(g17)
    c: Equal(g0,g11)
    c: Equal(g11,g5)
    c: Equal(g5,g14)
    c: DistanceY(g11,g11) = 30
    c: Symmetric(g18,g17,g24)
    c: Symmetric(g6,g4,g23)
    c: Symmetric(g16,g22,g16)
    c: Symmetric(g16,g18,g21)
    c: Symmetric(g8,g9,g21)
    c: Symmetric(g17,g16,g23)
    c: Symmetric(g12,g12,g24)
    c: Symmetric(g2,g1,g25)
    c: Symmetric(g16,g16,g25)
FEATURE [PartDesign::Pocket] Pocket004  label="Ausschnitte  Touch"
  BaseFeature = -> Pad
  Direction = (0,0,1)
  Length = 3.5
  Length2 = 100
  Profile = -> Sketch005
  Type = 0
FEATURE [PartDesign::Fillet] Fillet
  Base = -> Pocket004 [Edge3,Edge20,Edge6,Edge1]
  BaseFeature = -> Pocket004
  Radius = 7.5
  SupportTransform = false
FEATURE [Sketcher::SketchObject] Sketch
  ExternalGeometry = -> [Fillet]
  FullyConstrained = true
  MapMode = 5
  Placement = pos=(0,0,0) rot=(1,0,0;3.14159rad)
  Support = -> [Fillet]
  sketch-geometry (9):
    g0: LineSegment StartX=7.5 StartY=-7.5 StartZ=0 EndX=122.5 EndY=-7.5 EndZ=0
    g1: LineSegment StartX=122.5 StartY=-7.5 StartZ=0 EndX=122.5 EndY=-77.5 EndZ=0
    g2: LineSegment StartX=122.5 StartY=-77.5 StartZ=0 EndX=7.5 EndY=-77.5 EndZ=0
    g3: LineSegment StartX=7.5 StartY=-77.5 StartZ=0 EndX=7.5 EndY=-7.5 EndZ=0
    g4: GeomPoint X=65 Y=-42.5 Z=0
    g5: Circle CenterX=122.5 CenterY=-7.5 CenterZ=0 NormalX=0 NormalY=0 NormalZ=1 AngleXU=0 Radius=2.8
    g6: Circle CenterX=122.5 CenterY=-77.5 CenterZ=0 NormalX=0 NormalY=0 NormalZ=1 AngleXU=0 Radius=2.8
    g7: Circle CenterX=7.5 CenterY=-77.5 CenterZ=0 NormalX=0 NormalY=0 NormalZ=1 AngleXU=0 Radius=2.8
    g8: Circle CenterX=7.5 CenterY=-7.5 CenterZ=0 NormalX=0 NormalY=0 NormalZ=1 AngleXU=0 Radius=2.8
  constraints (19):
    c: Coincident(g0,g1)
    c: Coincident(g1,g2)
    c: Coincident(g2,g3)
    c: Coincident(g3,g0)
    c: Horizontal(g0)
    c: Horizontal(g2)
    c: Vertical(g1)
    c: Vertical(g3)
    c: Symmetric(g2,g0,g4)
    c: Coincident(g5,g0)
    c: Coincident(g6,g1)
    c: Coincident(g7,g2)
    c: Diameter(g7) = 5.6
    c: Equal(g5,g6)
    c: Equal(g6,g7)
    c: Equal(g7,g8)
    c: Symmetric(g-4,g-5,g4)
    c: Coincident(g0,g8)
    c: Coincident(g8,g-6)
FEATURE [PartDesign::Pocket] Pocket
  BaseFeature = -> Fillet
  Direction = (0,0,1)
  Length = 10
  Length2 = 5
  Profile = -> Sketch
  ReferenceAxis = -> Sketch [N_Axis]
  Type = 0
FEATURE [PartDesign::CoordinateSystem] LCS_2
  AttacherType = Attacher::AttachEngine3D
  AttachmentOffset = pos=(0,0,0) rot=(1,0,0;3.14159rad)
  MapMode = 5
  Support = -> [Pocket]
FEATURE [Sketcher::SketchObject] Sketch008
  ExternalGeometry = -> [Pocket]
  FullyConstrained = true
  MapMode = 5
  Placement = pos=(0,0,16) rot=(1,0,0;3.14159rad)
  Support = -> [Pocket]
  sketch-geometry (11):
    g0: LineSegment StartX=8 StartY=-42.6678 StartZ=0 EndX=28 EndY=-42.6678 EndZ=0
    g1: LineSegment StartX=28 StartY=-42.6678 StartZ=0 EndX=28 EndY=-67.1678 EndZ=0
    g2: LineSegment StartX=28 StartY=-67.1678 StartZ=0 EndX=8 EndY=-67.1678 EndZ=0
    g3: LineSegment StartX=8 StartY=-67.1678 StartZ=0 EndX=8 EndY=-42.6678 EndZ=0
    g4: GeomPoint X=8 Y=-42.6678 Z=0
    g5: GeomPoint X=4 Y=-42.6678 Z=0
    g6: LineSegment StartX=4 StartY=-42.6678 StartZ=0 EndX=8 EndY=-42.6678 EndZ=0
    g7: LineSegment StartX=6 StartY=-26.8322 StartZ=0 EndX=36.5 EndY=-26.8322 EndZ=0
    g8: LineSegment StartX=36.5 StartY=-26.8322 StartZ=0 EndX=36.5 EndY=-37.8322 EndZ=0
    g9: LineSegment StartX=36.5 StartY=-37.8322 StartZ=0 EndX=6 EndY=-37.8322 EndZ=0
    g10: LineSegment StartX=6 StartY=-37.8322 StartZ=0 EndX=6 EndY=-26.8322 EndZ=0
  constraints (29):
    c: Coincident(g0,g1)
    c: Coincident(g1,g2)
    c: Coincident(g2,g3)
    c: Coincident(g3,g0)
    c: Horizontal(g0)
    c: Horizontal(g2)
    c: Vertical(g1)
    c: Vertical(g3)
    c: DistanceX(g0,g0) = 20
    c: Coincident(g6,g5)
    c: Coincident(g6,g4)
    c: Horizontal(g6)
    c: DistanceX(g6,g6) = 4
    c: DistanceY(g3,g3) = 24.5
    c: Coincident(g0,g4)
    c: Coincident(g7,g8)
    c: Coincident(g8,g9)
    c: Coincident(g9,g10)
    c: Coincident(g10,g7)
    c: Horizontal(g7)
    c: Horizontal(g9)
    c: Vertical(g8)
    c: Vertical(g10)
    c: DistanceX(g7,g7) = 30.5
    c: DistanceY(g8,g8) = 11
    c: PointOnObject(g5,g-3)
    c: DistanceX(g-3,g7) = 2
    c: DistanceY(g7,g-3) = 11
    c: DistanceY(g-3,g2) = 2
FEATURE [PartDesign::Pocket] Pocket006
  BaseFeature = -> Pocket
  Direction = (0,0,1)
  Length = 2
  Length2 = 5
  Profile = -> Sketch008
  ReferenceAxis = -> Sketch008 [N_Axis]
  Refine = true
  Type = 0
FEATURE [Sketcher::SketchObject] Sketch007
  ExternalGeometry = -> [Pocket004,Sketch003]
  FullyConstrained = true
  MapMode = 5
  Placement = pos=(0,0,19) rot=(1,0,0;3.14159rad)
  Support = -> [Pocket004]
  sketch-geometry (5):
    g0: Circle CenterX=51.5 CenterY=-59 CenterZ=0 NormalX=0 NormalY=0 NormalZ=1 AngleXU=0 Radius=1.35
    g1: Circle CenterX=78.5 CenterY=-59 CenterZ=0 NormalX=0 NormalY=0 NormalZ=1 AngleXU=0 Radius=1.35
    g2: LineSegment StartX=51.5 StartY=-59 StartZ=0 EndX=78.5 EndY=-59 EndZ=0
    g3: LineSegment StartX=65 StartY=-56 StartZ=0 EndX=65 EndY=-62 EndZ=0
    g4: GeomPoint X=65 Y=-59 Z=0
  constraints (11):
    c: Coincident(g2,g0)
    c: Coincident(g2,g1)
    c: Horizontal(g2)
    c: Equal(g1,g0)
    c: Diameter(g0) = 2.7
    c: DistanceX(g2,g2) = 27
    c: Vertical(g3)
    c: Symmetric(g0,g1,g4)
    c: Symmetric(g3,g3,g4)
    c: Symmetric(g-5,g-5,g3)
    c: PointOnObject(g3,g-6)
FEATURE [PartDesign::Body] Body002  label="Front"
  Group = -> [Box002,Sketch001,Pocket001,Sketch002,Pocket002,Sketch003,Pocket003,Sketch004,Pad,Sketch005,Pocket004,Sketch007,Sketch008,Fillet,Sketch,Pocket,LCS_2,Pocket006]
  Origin = -> Origin002
  Tip = -> Pocket006
COMPONENT P4 — geometry summary ("Tela OLed 128x64 v15"; no construction recipe available for this part):
  bounding box: 28.3 x 27.6 x 10.4 mm
  tessellated surface: 4,433 triangles
  volume: 2103 mm^3 (26% of its bounding box)
  symmetry: mirror-symmetric across its x mid-plane
PROVENANCE & LICENSES
A FreeCAD (.FCStd) document from a public repository crawl; recipes are the document's own serialized feature recipes (and, for linked parts, companion documents' recipes).
License: as declared in the source repository (recorded in the dataset sidecar).
